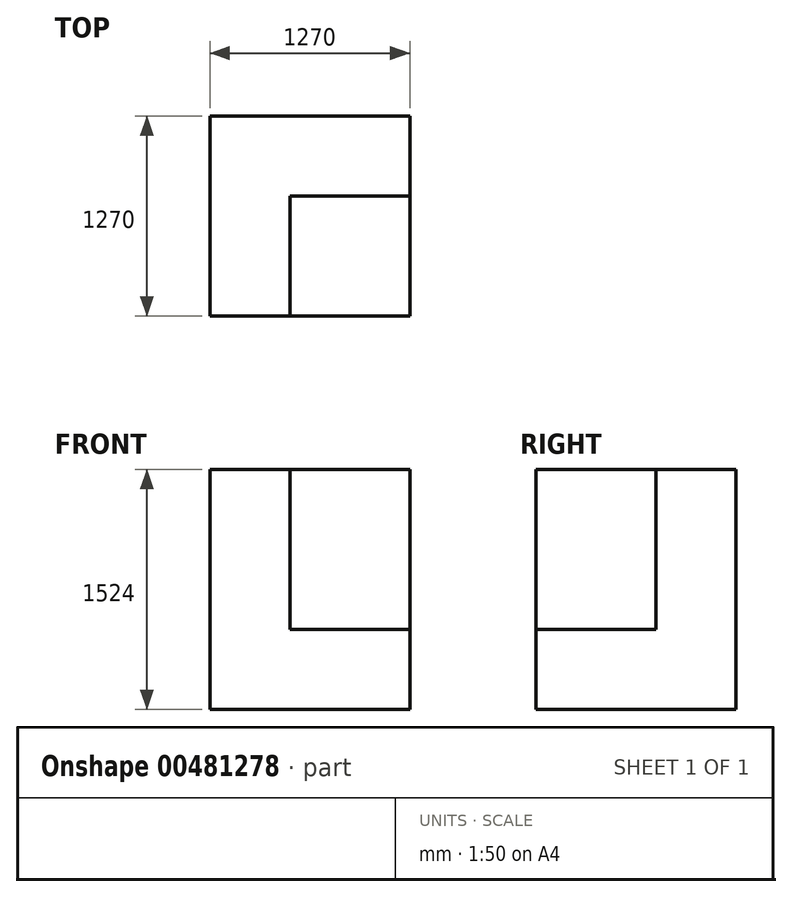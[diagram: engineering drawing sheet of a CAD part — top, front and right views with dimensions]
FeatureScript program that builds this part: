
annotation { "Feature Type Name" : "Feature", "Feature Type Description" : "" }
export const myFeature = defineFeature(function(context is Context, id is Id, definition is map)
    precondition{}
    {
        {
            var Q0;
            Q0=qCreatedBy(makeId("Front.planeOp"),FACE);
            var sketch = newSketch(context, id + "F0", { "sketchPlane" : qUnion([Q0])});
            skLineSegment(sketch, "E0", {"start": v(0, 0) * mm, "end": v(0, 1524) * mm});
            skLineSegment(sketch, "E1", {"start": v(0, 1524) * mm, "end": v(508, 1524) * mm});
            skLineSegment(sketch, "E2", {"start": v(508, 1524) * mm, "end": v(508, 508) * mm});
            skLineSegment(sketch, "E3", {"start": v(508, 508) * mm, "end": v(1270, 508) * mm});
            skLineSegment(sketch, "E4", {"start": v(1270, 508) * mm, "end": v(1270, 0) * mm});
            skLineSegment(sketch, "E5", {"start": v(0, 0) * mm, "end": v(1270, 0) * mm});
            skSolve(sketch);
        }
        {
            var Q0;
            Q0=makeQuery(id+"F0.imprint","IMPRINT",FACE,{"disambiguationData":[TD([[makeQuery(id+"F0.imprint","IMPRINT",EDGE,{"derivedFrom":sQuery(id+"F0.wireOp",EDGE,"E0")}),-1.0]])]});
            extrude(context, id + "F1", {"entities" : qUnion([Q0]), "depth" : 1270 * mm});
        }
        {
            var Q0;
            Q0=makeQuery(id+"F1.opExtrude","CAP_FACE",FACE,{"disambiguationData":[OSD([sQuery(id+"F0.wireOp",EDGE,"E0"),sQuery(id+"F0.wireOp",EDGE,"E1"),sQuery(id+"F0.wireOp",EDGE,"E2"),sQuery(id+"F0.wireOp",EDGE,"E3"),sQuery(id+"F0.wireOp",EDGE,"E4"),sQuery(id+"F0.wireOp",EDGE,"E5")])],"isStart":true});
            var sketch = newSketch(context, id + "F2", { "sketchPlane" : qUnion([Q0])});
            skLineSegment(sketch, "E6", {"start": v(-508, 1524) * mm, "end": v(-1270, 1524) * mm});
            skLineSegment(sketch, "E7", {"start": v(-1270, 1524) * mm, "end": v(-1270, 508) * mm});
            skLineSegment(sketch, "E8", {"start": v(-1270, 508) * mm, "end": v(-508, 508) * mm});
            skLineSegment(sketch, "E9", {"start": v(-508, 508) * mm, "end": v(-508, 1524) * mm});
            skSolve(sketch);
        }
        {
            var Q0;
            Q0 = qSketchRegion(id + "F2", true);
            extrude(context, id + "F3", {"entities" : qUnion([Q0]), "operationType" : NewBodyOperationType.ADD, "oppositeDirection" : true, "depth" : 508 * mm});
        }
    });
